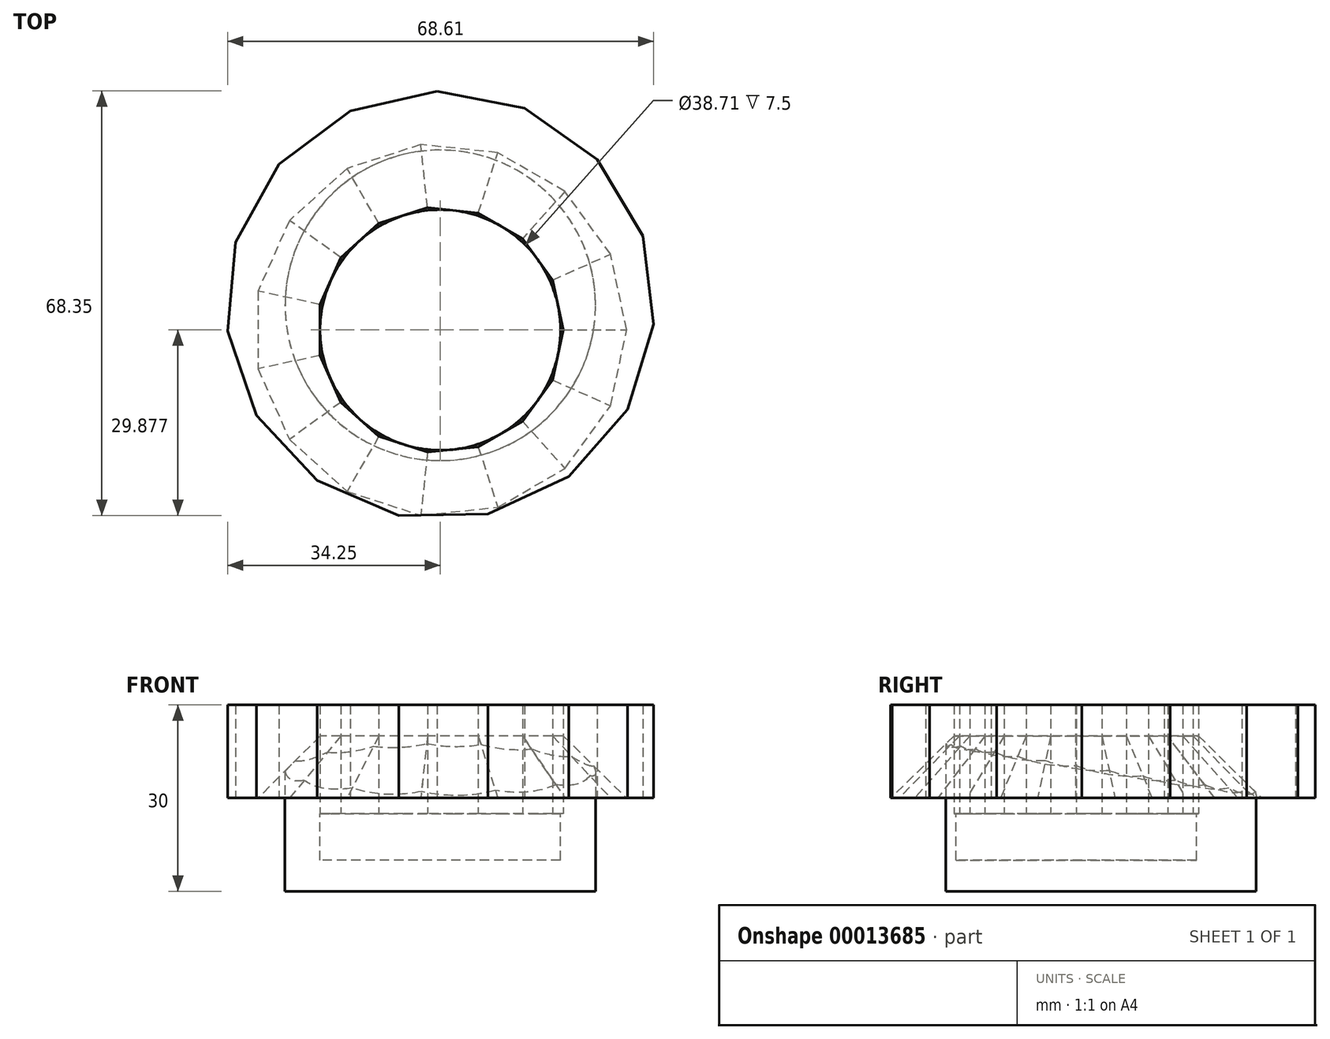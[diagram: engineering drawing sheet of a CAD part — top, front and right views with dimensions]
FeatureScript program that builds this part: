
annotation { "Feature Type Name" : "Feature", "Feature Type Description" : "" }
export const myFeature = defineFeature(function(context is Context, id is Id, definition is map)
    precondition{}
    {
        {
            var Q0;
            Q0=qCreatedBy(makeId("Top.planeOp"),FACE);
            var sketch = newSketch(context, id + "F0", { "sketchPlane" : qUnion([Q0])});
            skCircle(sketch, "E0", {"center": v(0, 0) * mm, "radius": 25 * mm});
            skSolve(sketch);
        }
        {
            var Q0;
            Q0 = qSketchRegion(id + "F0", true);
            extrude(context, id + "F1", {"entities" : qUnion([Q0]), "depth" : 25 * mm});
        }
        {
            var Q0;
            Q0=makeQuery(id+"F1.opExtrude","CAP_FACE",FACE,{"disambiguationData":[OSD([sQuery(id+"F0.wireOp",EDGE,"E0")])],"isStart":false});
            var sketch = newSketch(context, id + "F2", { "sketchPlane" : qUnion([Q0])});
            skCircle(sketch, "E1", {"center": v(0, -3.97) * mm, "radius": 19.36 * mm});
            skSolve(sketch);
        }
        {
            var Q0;
            Q0 = qSketchRegion(id + "F2", true);
            extrude(context, id + "F3", {"entities" : qUnion([Q0]), "operationType" : NewBodyOperationType.REMOVE, "oppositeDirection" : true, "depth" : 20 * mm});
        }
        {
            var Q0;
            Q0=qCreatedBy(makeId("Top.planeOp"),FACE);
            cPlane(context, id + "F4", {"entities" : qUnion([Q0]), "cplaneType" : CPlaneType.OFFSET, "offset" : 15 * mm, "width" : 150 * mm, "height" : 150 * mm});
        }
        {
            var Q0;
            Q0=qCreatedBy(id+"F4.planeOp",FACE);
            var sketch = newSketch(context, id + "F5", { "sketchPlane" : qUnion([Q0])});
            skCircle(sketch, "E2.cCircle", {"center": v(0, 0) * mm, "radius": 33.75 * mm, "construction": true});
            skLineSegment(sketch, "E2.0", {"start": v(-32.97, 10.16) * mm, "end": v(-25.99, 22.7) * mm});
            skLineSegment(sketch, "E2.1", {"start": v(-25.99, 22.7) * mm, "end": v(-14.5, 31.3) * mm});
            skLineSegment(sketch, "E2.2", {"start": v(-14.5, 31.3) * mm, "end": v(-0.52, 34.5) * mm});
            skLineSegment(sketch, "E2.3", {"start": v(-0.52, 34.5) * mm, "end": v(13.55, 31.73) * mm});
            skLineSegment(sketch, "E2.4", {"start": v(13.55, 31.73) * mm, "end": v(25.29, 23.47) * mm});
            skLineSegment(sketch, "E2.5", {"start": v(25.29, 23.47) * mm, "end": v(32.65, 11.16) * mm});
            skLineSegment(sketch, "E2.6", {"start": v(32.65, 11.16) * mm, "end": v(34.36, -3.09) * mm});
            skLineSegment(sketch, "E2.7", {"start": v(34.36, -3.09) * mm, "end": v(30.14, -16.8) * mm});
            skLineSegment(sketch, "E2.8", {"start": v(30.14, -16.8) * mm, "end": v(20.7, -27.6) * mm});
            skLineSegment(sketch, "E2.9", {"start": v(20.7, -27.6) * mm, "end": v(7.68, -33.63) * mm});
            skLineSegment(sketch, "E2.10", {"start": v(7.68, -33.63) * mm, "end": v(-6.66, -33.85) * mm});
            skLineSegment(sketch, "E2.11", {"start": v(-6.66, -33.85) * mm, "end": v(-19.85, -28.22) * mm});
            skLineSegment(sketch, "E2.12", {"start": v(-19.85, -28.22) * mm, "end": v(-29.61, -17.7) * mm});
            skLineSegment(sketch, "E2.13", {"start": v(-29.61, -17.7) * mm, "end": v(-34.25, -4.13) * mm});
            skLineSegment(sketch, "E2.14", {"start": v(-34.25, -4.13) * mm, "end": v(-32.97, 10.16) * mm});
            skPoint(sketch, "E2.0.midPoint", {"position": v(-29.48, 16.43) * mm});
            skSolve(sketch);
        }
        {
            var Q0;
            Q0=makeQuery(id+"F1.opExtrude","CAP_FACE",FACE,{"disambiguationData":[OSD([sQuery(id+"F0.wireOp",EDGE,"E0")])],"isStart":false});
            var sketch = newSketch(context, id + "F6", { "sketchPlane" : qUnion([Q0])});
            skCircle(sketch, "E3.cCircle", {"center": v(0, -3.97) * mm, "radius": 19.36 * mm, "construction": true});
            skLineSegment(sketch, "E3.0", {"start": v(-19.36, -8.09) * mm, "end": v(-19.36, 0.14) * mm});
            skLineSegment(sketch, "E3.1", {"start": v(-19.36, 0.14) * mm, "end": v(-16.01, 7.66) * mm});
            skLineSegment(sketch, "E3.2", {"start": v(-16.01, 7.66) * mm, "end": v(-9.9, 13.17) * mm});
            skLineSegment(sketch, "E3.3", {"start": v(-9.9, 13.17) * mm, "end": v(-2.07, 15.7) * mm});
            skLineSegment(sketch, "E3.4", {"start": v(-2.07, 15.7) * mm, "end": v(6.12, 14.85) * mm});
            skLineSegment(sketch, "E3.5", {"start": v(6.12, 14.85) * mm, "end": v(13.24, 10.73) * mm});
            skLineSegment(sketch, "E3.6", {"start": v(13.24, 10.73) * mm, "end": v(18.08, 4.08) * mm});
            skLineSegment(sketch, "E3.7", {"start": v(18.08, 4.08) * mm, "end": v(19.79, -3.97) * mm});
            skLineSegment(sketch, "E3.8", {"start": v(19.79, -3.97) * mm, "end": v(18.08, -12.02) * mm});
            skLineSegment(sketch, "E3.9", {"start": v(18.08, -12.02) * mm, "end": v(13.24, -18.68) * mm});
            skLineSegment(sketch, "E3.10", {"start": v(13.24, -18.68) * mm, "end": v(6.12, -22.8) * mm});
            skLineSegment(sketch, "E3.11", {"start": v(6.12, -22.8) * mm, "end": v(-2.07, -23.65) * mm});
            skLineSegment(sketch, "E3.12", {"start": v(-2.07, -23.65) * mm, "end": v(-9.9, -21.11) * mm});
            skLineSegment(sketch, "E3.13", {"start": v(-9.9, -21.11) * mm, "end": v(-16.01, -15.6) * mm});
            skLineSegment(sketch, "E3.14", {"start": v(-16.01, -15.6) * mm, "end": v(-19.36, -8.09) * mm});
            skPoint(sketch, "E3.0.midPoint", {"position": v(-19.36, -3.97) * mm});
            skSolve(sketch);
        }
        {
            var Q0;
            Q0 = qSketchRegion(id + "F5", true);
            extrude(context, id + "F7", {"entities" : qUnion([Q0]), "depth" : 15 * mm});
        }
        {
            var Q0;
            Q0 = qSketchRegion(id + "F6", true);
            extrude(context, id + "F8", {"entities" : qUnion([Q0]), "operationType" : NewBodyOperationType.REMOVE, "endBound" : BoundingType.SYMMETRIC, "depth" : 25 * mm});
        }
        {
            var Q0;
            Q0=makeQuery(id+"F8.boolean.opBoolean","INTERSECT",EDGE,{"derivedFrom":[makeQuery(id+"F7.opExtrude","CAP_FACE",FACE,{"disambiguationData":[OSD([sQuery(id+"F5.wireOp",EDGE,"E2.0"),sQuery(id+"F5.wireOp",EDGE,"E2.1"),sQuery(id+"F5.wireOp",EDGE,"E2.2"),sQuery(id+"F5.wireOp",EDGE,"E2.3"),sQuery(id+"F5.wireOp",EDGE,"E2.4"),sQuery(id+"F5.wireOp",EDGE,"E2.5"),sQuery(id+"F5.wireOp",EDGE,"E2.6"),sQuery(id+"F5.wireOp",EDGE,"E2.7"),sQuery(id+"F5.wireOp",EDGE,"E2.8"),sQuery(id+"F5.wireOp",EDGE,"E2.9"),sQuery(id+"F5.wireOp",EDGE,"E2.10"),sQuery(id+"F5.wireOp",EDGE,"E2.11"),sQuery(id+"F5.wireOp",EDGE,"E2.12"),sQuery(id+"F5.wireOp",EDGE,"E2.13"),sQuery(id+"F5.wireOp",EDGE,"E2.14")])],"isStart":true}),makeQuery(id+"F8.opExtrude","SWEPT_FACE",FACE,{"disambiguationData":[OSD([sQuery(id+"F6.wireOp",EDGE,"E3.5")])]})]});
            var Q1;
            Q1=makeQuery(id+"F8.boolean.opBoolean","INTERSECT",EDGE,{"derivedFrom":[makeQuery(id+"F7.opExtrude","CAP_FACE",FACE,{"disambiguationData":[OSD([sQuery(id+"F5.wireOp",EDGE,"E2.0"),sQuery(id+"F5.wireOp",EDGE,"E2.1"),sQuery(id+"F5.wireOp",EDGE,"E2.2"),sQuery(id+"F5.wireOp",EDGE,"E2.3"),sQuery(id+"F5.wireOp",EDGE,"E2.4"),sQuery(id+"F5.wireOp",EDGE,"E2.5"),sQuery(id+"F5.wireOp",EDGE,"E2.6"),sQuery(id+"F5.wireOp",EDGE,"E2.7"),sQuery(id+"F5.wireOp",EDGE,"E2.8"),sQuery(id+"F5.wireOp",EDGE,"E2.9"),sQuery(id+"F5.wireOp",EDGE,"E2.10"),sQuery(id+"F5.wireOp",EDGE,"E2.11"),sQuery(id+"F5.wireOp",EDGE,"E2.12"),sQuery(id+"F5.wireOp",EDGE,"E2.13"),sQuery(id+"F5.wireOp",EDGE,"E2.14")])],"isStart":true}),makeQuery(id+"F8.opExtrude","SWEPT_FACE",FACE,{"disambiguationData":[OSD([sQuery(id+"F6.wireOp",EDGE,"E3.4")])]})]});
            var Q2;
            Q2=makeQuery(id+"F8.boolean.opBoolean","INTERSECT",EDGE,{"derivedFrom":[makeQuery(id+"F7.opExtrude","CAP_FACE",FACE,{"disambiguationData":[OSD([sQuery(id+"F5.wireOp",EDGE,"E2.0"),sQuery(id+"F5.wireOp",EDGE,"E2.1"),sQuery(id+"F5.wireOp",EDGE,"E2.2"),sQuery(id+"F5.wireOp",EDGE,"E2.3"),sQuery(id+"F5.wireOp",EDGE,"E2.4"),sQuery(id+"F5.wireOp",EDGE,"E2.5"),sQuery(id+"F5.wireOp",EDGE,"E2.6"),sQuery(id+"F5.wireOp",EDGE,"E2.7"),sQuery(id+"F5.wireOp",EDGE,"E2.8"),sQuery(id+"F5.wireOp",EDGE,"E2.9"),sQuery(id+"F5.wireOp",EDGE,"E2.10"),sQuery(id+"F5.wireOp",EDGE,"E2.11"),sQuery(id+"F5.wireOp",EDGE,"E2.12"),sQuery(id+"F5.wireOp",EDGE,"E2.13"),sQuery(id+"F5.wireOp",EDGE,"E2.14")])],"isStart":true}),makeQuery(id+"F8.opExtrude","SWEPT_FACE",FACE,{"disambiguationData":[OSD([sQuery(id+"F6.wireOp",EDGE,"E3.3")])]})]});
            var Q3;
            Q3=makeQuery(id+"F8.boolean.opBoolean","INTERSECT",EDGE,{"derivedFrom":[makeQuery(id+"F7.opExtrude","CAP_FACE",FACE,{"disambiguationData":[OSD([sQuery(id+"F5.wireOp",EDGE,"E2.0"),sQuery(id+"F5.wireOp",EDGE,"E2.1"),sQuery(id+"F5.wireOp",EDGE,"E2.2"),sQuery(id+"F5.wireOp",EDGE,"E2.3"),sQuery(id+"F5.wireOp",EDGE,"E2.4"),sQuery(id+"F5.wireOp",EDGE,"E2.5"),sQuery(id+"F5.wireOp",EDGE,"E2.6"),sQuery(id+"F5.wireOp",EDGE,"E2.7"),sQuery(id+"F5.wireOp",EDGE,"E2.8"),sQuery(id+"F5.wireOp",EDGE,"E2.9"),sQuery(id+"F5.wireOp",EDGE,"E2.10"),sQuery(id+"F5.wireOp",EDGE,"E2.11"),sQuery(id+"F5.wireOp",EDGE,"E2.12"),sQuery(id+"F5.wireOp",EDGE,"E2.13"),sQuery(id+"F5.wireOp",EDGE,"E2.14")])],"isStart":true}),makeQuery(id+"F8.opExtrude","SWEPT_FACE",FACE,{"disambiguationData":[OSD([sQuery(id+"F6.wireOp",EDGE,"E3.2")])]})]});
            var Q4;
            Q4=makeQuery(id+"F8.boolean.opBoolean","INTERSECT",EDGE,{"derivedFrom":[makeQuery(id+"F7.opExtrude","CAP_FACE",FACE,{"disambiguationData":[OSD([sQuery(id+"F5.wireOp",EDGE,"E2.0"),sQuery(id+"F5.wireOp",EDGE,"E2.1"),sQuery(id+"F5.wireOp",EDGE,"E2.2"),sQuery(id+"F5.wireOp",EDGE,"E2.3"),sQuery(id+"F5.wireOp",EDGE,"E2.4"),sQuery(id+"F5.wireOp",EDGE,"E2.5"),sQuery(id+"F5.wireOp",EDGE,"E2.6"),sQuery(id+"F5.wireOp",EDGE,"E2.7"),sQuery(id+"F5.wireOp",EDGE,"E2.8"),sQuery(id+"F5.wireOp",EDGE,"E2.9"),sQuery(id+"F5.wireOp",EDGE,"E2.10"),sQuery(id+"F5.wireOp",EDGE,"E2.11"),sQuery(id+"F5.wireOp",EDGE,"E2.12"),sQuery(id+"F5.wireOp",EDGE,"E2.13"),sQuery(id+"F5.wireOp",EDGE,"E2.14")])],"isStart":true}),makeQuery(id+"F8.opExtrude","SWEPT_FACE",FACE,{"disambiguationData":[OSD([sQuery(id+"F6.wireOp",EDGE,"E3.1")])]})]});
            var Q5;
            Q5=makeQuery(id+"F8.boolean.opBoolean","INTERSECT",EDGE,{"derivedFrom":[makeQuery(id+"F7.opExtrude","CAP_FACE",FACE,{"disambiguationData":[OSD([sQuery(id+"F5.wireOp",EDGE,"E2.0"),sQuery(id+"F5.wireOp",EDGE,"E2.1"),sQuery(id+"F5.wireOp",EDGE,"E2.2"),sQuery(id+"F5.wireOp",EDGE,"E2.3"),sQuery(id+"F5.wireOp",EDGE,"E2.4"),sQuery(id+"F5.wireOp",EDGE,"E2.5"),sQuery(id+"F5.wireOp",EDGE,"E2.6"),sQuery(id+"F5.wireOp",EDGE,"E2.7"),sQuery(id+"F5.wireOp",EDGE,"E2.8"),sQuery(id+"F5.wireOp",EDGE,"E2.9"),sQuery(id+"F5.wireOp",EDGE,"E2.10"),sQuery(id+"F5.wireOp",EDGE,"E2.11"),sQuery(id+"F5.wireOp",EDGE,"E2.12"),sQuery(id+"F5.wireOp",EDGE,"E2.13"),sQuery(id+"F5.wireOp",EDGE,"E2.14")])],"isStart":true}),makeQuery(id+"F8.opExtrude","SWEPT_FACE",FACE,{"disambiguationData":[OSD([sQuery(id+"F6.wireOp",EDGE,"E3.0")])]})]});
            var Q6;
            Q6=makeQuery(id+"F8.boolean.opBoolean","INTERSECT",EDGE,{"derivedFrom":[makeQuery(id+"F7.opExtrude","CAP_FACE",FACE,{"disambiguationData":[OSD([sQuery(id+"F5.wireOp",EDGE,"E2.0"),sQuery(id+"F5.wireOp",EDGE,"E2.1"),sQuery(id+"F5.wireOp",EDGE,"E2.2"),sQuery(id+"F5.wireOp",EDGE,"E2.3"),sQuery(id+"F5.wireOp",EDGE,"E2.4"),sQuery(id+"F5.wireOp",EDGE,"E2.5"),sQuery(id+"F5.wireOp",EDGE,"E2.6"),sQuery(id+"F5.wireOp",EDGE,"E2.7"),sQuery(id+"F5.wireOp",EDGE,"E2.8"),sQuery(id+"F5.wireOp",EDGE,"E2.9"),sQuery(id+"F5.wireOp",EDGE,"E2.10"),sQuery(id+"F5.wireOp",EDGE,"E2.11"),sQuery(id+"F5.wireOp",EDGE,"E2.12"),sQuery(id+"F5.wireOp",EDGE,"E2.13"),sQuery(id+"F5.wireOp",EDGE,"E2.14")])],"isStart":true}),makeQuery(id+"F8.opExtrude","SWEPT_FACE",FACE,{"disambiguationData":[OSD([sQuery(id+"F6.wireOp",EDGE,"E3.14")])]})]});
            var Q7;
            Q7=makeQuery(id+"F8.boolean.opBoolean","INTERSECT",EDGE,{"derivedFrom":[makeQuery(id+"F7.opExtrude","CAP_FACE",FACE,{"disambiguationData":[OSD([sQuery(id+"F5.wireOp",EDGE,"E2.0"),sQuery(id+"F5.wireOp",EDGE,"E2.1"),sQuery(id+"F5.wireOp",EDGE,"E2.2"),sQuery(id+"F5.wireOp",EDGE,"E2.3"),sQuery(id+"F5.wireOp",EDGE,"E2.4"),sQuery(id+"F5.wireOp",EDGE,"E2.5"),sQuery(id+"F5.wireOp",EDGE,"E2.6"),sQuery(id+"F5.wireOp",EDGE,"E2.7"),sQuery(id+"F5.wireOp",EDGE,"E2.8"),sQuery(id+"F5.wireOp",EDGE,"E2.9"),sQuery(id+"F5.wireOp",EDGE,"E2.10"),sQuery(id+"F5.wireOp",EDGE,"E2.11"),sQuery(id+"F5.wireOp",EDGE,"E2.12"),sQuery(id+"F5.wireOp",EDGE,"E2.13"),sQuery(id+"F5.wireOp",EDGE,"E2.14")])],"isStart":true}),makeQuery(id+"F8.opExtrude","SWEPT_FACE",FACE,{"disambiguationData":[OSD([sQuery(id+"F6.wireOp",EDGE,"E3.13")])]})]});
            var Q8;
            Q8=makeQuery(id+"F8.boolean.opBoolean","INTERSECT",EDGE,{"derivedFrom":[makeQuery(id+"F7.opExtrude","CAP_FACE",FACE,{"disambiguationData":[OSD([sQuery(id+"F5.wireOp",EDGE,"E2.0"),sQuery(id+"F5.wireOp",EDGE,"E2.1"),sQuery(id+"F5.wireOp",EDGE,"E2.2"),sQuery(id+"F5.wireOp",EDGE,"E2.3"),sQuery(id+"F5.wireOp",EDGE,"E2.4"),sQuery(id+"F5.wireOp",EDGE,"E2.5"),sQuery(id+"F5.wireOp",EDGE,"E2.6"),sQuery(id+"F5.wireOp",EDGE,"E2.7"),sQuery(id+"F5.wireOp",EDGE,"E2.8"),sQuery(id+"F5.wireOp",EDGE,"E2.9"),sQuery(id+"F5.wireOp",EDGE,"E2.10"),sQuery(id+"F5.wireOp",EDGE,"E2.11"),sQuery(id+"F5.wireOp",EDGE,"E2.12"),sQuery(id+"F5.wireOp",EDGE,"E2.13"),sQuery(id+"F5.wireOp",EDGE,"E2.14")])],"isStart":true}),makeQuery(id+"F8.opExtrude","SWEPT_FACE",FACE,{"disambiguationData":[OSD([sQuery(id+"F6.wireOp",EDGE,"E3.11")])]})]});
            var Q9;
            Q9=makeQuery(id+"F8.boolean.opBoolean","INTERSECT",EDGE,{"derivedFrom":[makeQuery(id+"F7.opExtrude","CAP_FACE",FACE,{"disambiguationData":[OSD([sQuery(id+"F5.wireOp",EDGE,"E2.0"),sQuery(id+"F5.wireOp",EDGE,"E2.1"),sQuery(id+"F5.wireOp",EDGE,"E2.2"),sQuery(id+"F5.wireOp",EDGE,"E2.3"),sQuery(id+"F5.wireOp",EDGE,"E2.4"),sQuery(id+"F5.wireOp",EDGE,"E2.5"),sQuery(id+"F5.wireOp",EDGE,"E2.6"),sQuery(id+"F5.wireOp",EDGE,"E2.7"),sQuery(id+"F5.wireOp",EDGE,"E2.8"),sQuery(id+"F5.wireOp",EDGE,"E2.9"),sQuery(id+"F5.wireOp",EDGE,"E2.10"),sQuery(id+"F5.wireOp",EDGE,"E2.11"),sQuery(id+"F5.wireOp",EDGE,"E2.12"),sQuery(id+"F5.wireOp",EDGE,"E2.13"),sQuery(id+"F5.wireOp",EDGE,"E2.14")])],"isStart":true}),makeQuery(id+"F8.opExtrude","SWEPT_FACE",FACE,{"disambiguationData":[OSD([sQuery(id+"F6.wireOp",EDGE,"E3.12")])]})]});
            var Q10;
            Q10=makeQuery(id+"F8.boolean.opBoolean","INTERSECT",EDGE,{"derivedFrom":[makeQuery(id+"F7.opExtrude","CAP_FACE",FACE,{"disambiguationData":[OSD([sQuery(id+"F5.wireOp",EDGE,"E2.0"),sQuery(id+"F5.wireOp",EDGE,"E2.1"),sQuery(id+"F5.wireOp",EDGE,"E2.2"),sQuery(id+"F5.wireOp",EDGE,"E2.3"),sQuery(id+"F5.wireOp",EDGE,"E2.4"),sQuery(id+"F5.wireOp",EDGE,"E2.5"),sQuery(id+"F5.wireOp",EDGE,"E2.6"),sQuery(id+"F5.wireOp",EDGE,"E2.7"),sQuery(id+"F5.wireOp",EDGE,"E2.8"),sQuery(id+"F5.wireOp",EDGE,"E2.9"),sQuery(id+"F5.wireOp",EDGE,"E2.10"),sQuery(id+"F5.wireOp",EDGE,"E2.11"),sQuery(id+"F5.wireOp",EDGE,"E2.12"),sQuery(id+"F5.wireOp",EDGE,"E2.13"),sQuery(id+"F5.wireOp",EDGE,"E2.14")])],"isStart":true}),makeQuery(id+"F8.opExtrude","SWEPT_FACE",FACE,{"disambiguationData":[OSD([sQuery(id+"F6.wireOp",EDGE,"E3.10")])]})]});
            var Q11;
            Q11=makeQuery(id+"F8.boolean.opBoolean","INTERSECT",EDGE,{"derivedFrom":[makeQuery(id+"F7.opExtrude","CAP_FACE",FACE,{"disambiguationData":[OSD([sQuery(id+"F5.wireOp",EDGE,"E2.0"),sQuery(id+"F5.wireOp",EDGE,"E2.1"),sQuery(id+"F5.wireOp",EDGE,"E2.2"),sQuery(id+"F5.wireOp",EDGE,"E2.3"),sQuery(id+"F5.wireOp",EDGE,"E2.4"),sQuery(id+"F5.wireOp",EDGE,"E2.5"),sQuery(id+"F5.wireOp",EDGE,"E2.6"),sQuery(id+"F5.wireOp",EDGE,"E2.7"),sQuery(id+"F5.wireOp",EDGE,"E2.8"),sQuery(id+"F5.wireOp",EDGE,"E2.9"),sQuery(id+"F5.wireOp",EDGE,"E2.10"),sQuery(id+"F5.wireOp",EDGE,"E2.11"),sQuery(id+"F5.wireOp",EDGE,"E2.12"),sQuery(id+"F5.wireOp",EDGE,"E2.13"),sQuery(id+"F5.wireOp",EDGE,"E2.14")])],"isStart":true}),makeQuery(id+"F8.opExtrude","SWEPT_FACE",FACE,{"disambiguationData":[OSD([sQuery(id+"F6.wireOp",EDGE,"E3.9")])]})]});
            var Q12;
            Q12=makeQuery(id+"F8.boolean.opBoolean","INTERSECT",EDGE,{"derivedFrom":[makeQuery(id+"F7.opExtrude","CAP_FACE",FACE,{"disambiguationData":[OSD([sQuery(id+"F5.wireOp",EDGE,"E2.0"),sQuery(id+"F5.wireOp",EDGE,"E2.1"),sQuery(id+"F5.wireOp",EDGE,"E2.2"),sQuery(id+"F5.wireOp",EDGE,"E2.3"),sQuery(id+"F5.wireOp",EDGE,"E2.4"),sQuery(id+"F5.wireOp",EDGE,"E2.5"),sQuery(id+"F5.wireOp",EDGE,"E2.6"),sQuery(id+"F5.wireOp",EDGE,"E2.7"),sQuery(id+"F5.wireOp",EDGE,"E2.8"),sQuery(id+"F5.wireOp",EDGE,"E2.9"),sQuery(id+"F5.wireOp",EDGE,"E2.10"),sQuery(id+"F5.wireOp",EDGE,"E2.11"),sQuery(id+"F5.wireOp",EDGE,"E2.12"),sQuery(id+"F5.wireOp",EDGE,"E2.13"),sQuery(id+"F5.wireOp",EDGE,"E2.14")])],"isStart":true}),makeQuery(id+"F8.opExtrude","SWEPT_FACE",FACE,{"disambiguationData":[OSD([sQuery(id+"F6.wireOp",EDGE,"E3.8")])]})]});
            var Q13;
            Q13=makeQuery(id+"F8.boolean.opBoolean","INTERSECT",EDGE,{"derivedFrom":[makeQuery(id+"F7.opExtrude","CAP_FACE",FACE,{"disambiguationData":[OSD([sQuery(id+"F5.wireOp",EDGE,"E2.0"),sQuery(id+"F5.wireOp",EDGE,"E2.1"),sQuery(id+"F5.wireOp",EDGE,"E2.2"),sQuery(id+"F5.wireOp",EDGE,"E2.3"),sQuery(id+"F5.wireOp",EDGE,"E2.4"),sQuery(id+"F5.wireOp",EDGE,"E2.5"),sQuery(id+"F5.wireOp",EDGE,"E2.6"),sQuery(id+"F5.wireOp",EDGE,"E2.7"),sQuery(id+"F5.wireOp",EDGE,"E2.8"),sQuery(id+"F5.wireOp",EDGE,"E2.9"),sQuery(id+"F5.wireOp",EDGE,"E2.10"),sQuery(id+"F5.wireOp",EDGE,"E2.11"),sQuery(id+"F5.wireOp",EDGE,"E2.12"),sQuery(id+"F5.wireOp",EDGE,"E2.13"),sQuery(id+"F5.wireOp",EDGE,"E2.14")])],"isStart":true}),makeQuery(id+"F8.opExtrude","SWEPT_FACE",FACE,{"disambiguationData":[OSD([sQuery(id+"F6.wireOp",EDGE,"E3.7")])]})]});
            var Q14;
            Q14=makeQuery(id+"F8.boolean.opBoolean","INTERSECT",EDGE,{"derivedFrom":[makeQuery(id+"F7.opExtrude","CAP_FACE",FACE,{"disambiguationData":[OSD([sQuery(id+"F5.wireOp",EDGE,"E2.0"),sQuery(id+"F5.wireOp",EDGE,"E2.1"),sQuery(id+"F5.wireOp",EDGE,"E2.2"),sQuery(id+"F5.wireOp",EDGE,"E2.3"),sQuery(id+"F5.wireOp",EDGE,"E2.4"),sQuery(id+"F5.wireOp",EDGE,"E2.5"),sQuery(id+"F5.wireOp",EDGE,"E2.6"),sQuery(id+"F5.wireOp",EDGE,"E2.7"),sQuery(id+"F5.wireOp",EDGE,"E2.8"),sQuery(id+"F5.wireOp",EDGE,"E2.9"),sQuery(id+"F5.wireOp",EDGE,"E2.10"),sQuery(id+"F5.wireOp",EDGE,"E2.11"),sQuery(id+"F5.wireOp",EDGE,"E2.12"),sQuery(id+"F5.wireOp",EDGE,"E2.13"),sQuery(id+"F5.wireOp",EDGE,"E2.14")])],"isStart":true}),makeQuery(id+"F8.opExtrude","SWEPT_FACE",FACE,{"disambiguationData":[OSD([sQuery(id+"F6.wireOp",EDGE,"E3.6")])]})]});
            chamfer(context, id + "F9", {"entities" : qUnion([Q0, Q1, Q2, Q3, Q4, Q5, Q6, Q7, Q8, Q9, Q10, Q11, Q12, Q13, Q14]), "chamferType" : ChamferType.TWO_OFFSETS, "width1" : 10 * mm, "oppositeDirection" : false, "width2" : 10 * mm, "tangentPropagation" : true});
        }
        {
            var Q0;
            Q0=makeQuery(id+"F7.opExtrude","SWEPT_BODY",BODY,{"disambiguationData":[OSD([sQuery(id+"F5.wireOp",EDGE,"E2.0"),sQuery(id+"F5.wireOp",EDGE,"E2.1"),sQuery(id+"F5.wireOp",EDGE,"E2.2"),sQuery(id+"F5.wireOp",EDGE,"E2.3"),sQuery(id+"F5.wireOp",EDGE,"E2.4"),sQuery(id+"F5.wireOp",EDGE,"E2.5"),sQuery(id+"F5.wireOp",EDGE,"E2.6"),sQuery(id+"F5.wireOp",EDGE,"E2.7"),sQuery(id+"F5.wireOp",EDGE,"E2.8"),sQuery(id+"F5.wireOp",EDGE,"E2.9"),sQuery(id+"F5.wireOp",EDGE,"E2.10"),sQuery(id+"F5.wireOp",EDGE,"E2.11"),sQuery(id+"F5.wireOp",EDGE,"E2.12"),sQuery(id+"F5.wireOp",EDGE,"E2.13"),sQuery(id+"F5.wireOp",EDGE,"E2.14")])]});
            var Q1;
            Q1=makeQuery(id+"F1.opExtrude","SWEPT_BODY",BODY,{"disambiguationData":[OSD([sQuery(id+"F0.wireOp",EDGE,"E0")])]});
            booleanBodies(context, id + "F10", {"operationType" : BooleanOperationType.SUBTRACTION, "tools" : qUnion([Q0]), "targets" : qUnion([Q1]), "keepTools" : true});
        }
    });
